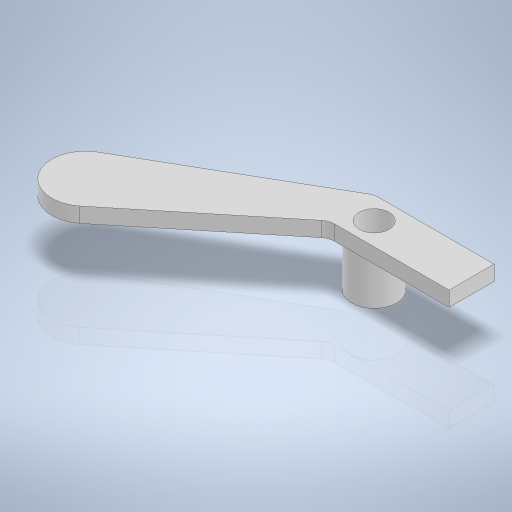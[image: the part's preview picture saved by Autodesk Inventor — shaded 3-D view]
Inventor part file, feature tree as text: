
AUTODESK INVENTOR PART (.ipt)
format: ipt  version: 2024 (Build 280153000, 153)  size: 269,312 bytes
history: native  units: mm
features: sketch x3, extrude x2, hole x1, fillet x1
ambient origin geometry x8: Origin, YZ Plane, XZ Plane, XY Plane, X Axis, Y Axis, Z Axis, Center Point
bodies: Volumenkörper1 (feature_tree)
feature tree (7):
  extrude  "Extrusion1"  TaperAngle=30.0deg  [1 undecoded]
  extrude  "Extrusion2"  Depth=16.0mm
  hole  "Bohrung1"  [1 undecoded]
  fillet  "Rundung1"  Radius=6.0mm
  sketch  "Skizze1"  dims[d1=6.0mm d3=30.0deg]
  sketch  "Skizze2"  dims[d4=4.5mm d5=16.0mm]
  sketch  "Skizze3"  dims[d6=27.0mm d7=2.0mm d8=0.0mm d9=6.0mm d10=13.0mm d11=6.0mm d12=0.0mm d13=4.0mm d14=6.0mm d15=4.0mm d16=2.0mm d17=90.0deg d18=8.0mm d19=20.594885mm d20=2.0mm]
note: 2 required parameter values undecoded (feature->parameter linkage not recoverable at this tier; creation-order binding heuristic only, values carry confidence <= 0.55)
